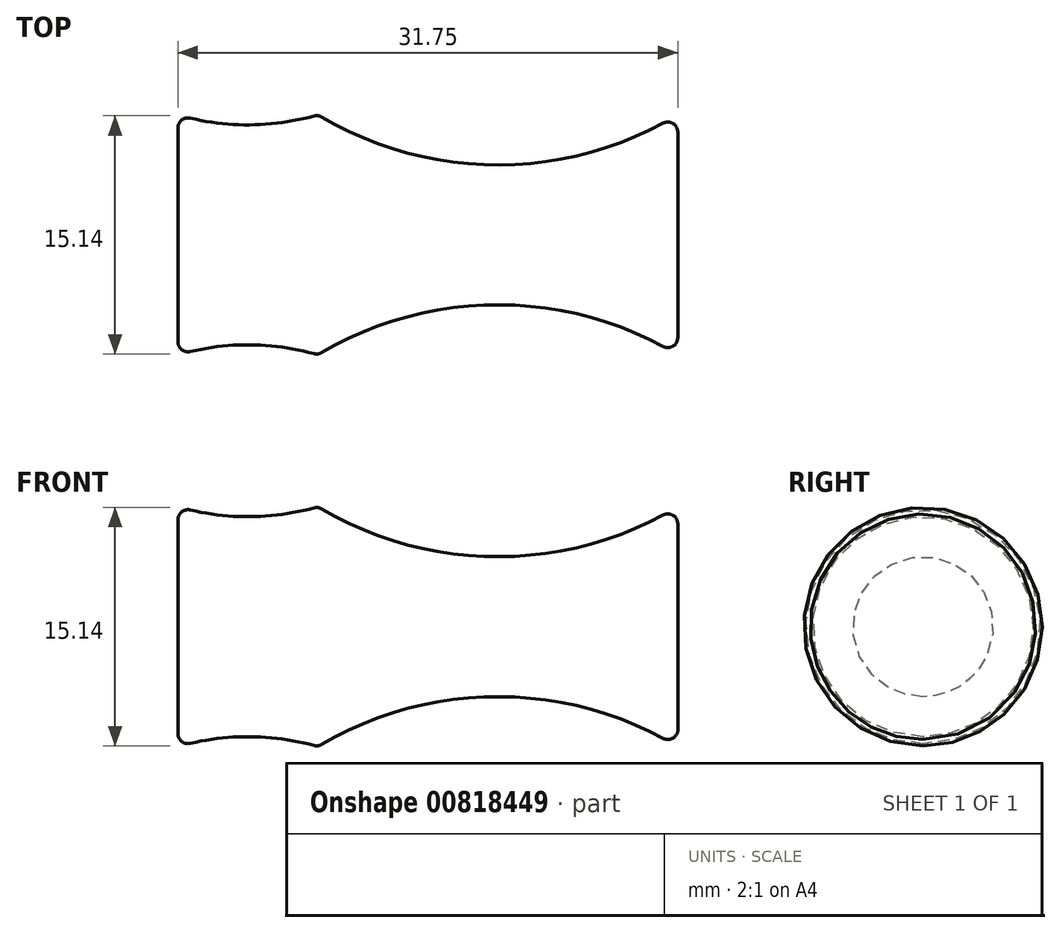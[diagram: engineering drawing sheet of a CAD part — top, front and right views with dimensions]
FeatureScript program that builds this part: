
annotation { "Feature Type Name" : "Feature", "Feature Type Description" : "" }
export const myFeature = defineFeature(function(context is Context, id is Id, definition is map)
    precondition{}
    {
        {
            var Q0;
            Q0=qCreatedBy(makeId("Top.planeOp"),FACE);
            var sketch = newSketch(context, id + "F0", { "sketchPlane" : qUnion([Q0])});
            skLineSegment(sketch, "E0", {"start": v(0, 0) * mm, "end": v(-31.75, 0) * mm});
            skLineSegment(sketch, "E1", {"start": v(-31.75, 0) * mm, "end": v(-31.75, 6.8) * mm});
            skArc(sketch, "E2", {"start": v(-30.97, 7.41) * mm, "mid": v(-27.03, 6.99) * mm, "end": v(-23.12, 7.55) * mm});
            skPoint(sketch, "E3.start.orphan", {"position": v(-27.3, 7.62) * mm});
            skLineSegment(sketch, "E4", {"start": v(0, 0) * mm, "end": v(0, 6.53) * mm});
            skLineSegment(sketch, "E5", {"start": v(-22.86, 7.62) * mm, "end": v(0, 7.62) * mm, "construction": true});
            skLineSegment(sketch, "E6", {"start": v(-11.43, 7.62) * mm, "end": v(-11.43, 4.44) * mm, "construction": true});
            skArc(sketch, "E7", {"start": v(-22.63, 7.48) * mm, "mid": v(-11.83, 4.45) * mm, "end": v(-0.94, 7.09) * mm});
            skPoint(sketch, "E8.visualSharp", {"position": v(0, 7.62) * mm});
            skArc(sketch, "E8.filletArc", {"start": v(0, 6.53) * mm, "mid": v(-0.3, 7.07) * mm, "end": v(-0.94, 7.09) * mm});
            skPoint(sketch, "E9.visualSharp", {"position": v(-22.86, 7.62) * mm});
            skArc(sketch, "E9.filletArc", {"start": v(-22.63, 7.48) * mm, "mid": v(-22.87, 7.56) * mm, "end": v(-23.12, 7.55) * mm});
            skPoint(sketch, "E10.visualSharp", {"position": v(-31.75, 7.62) * mm});
            skArc(sketch, "E10.filletArc", {"start": v(-30.97, 7.41) * mm, "mid": v(-31.5, 7.3) * mm, "end": v(-31.75, 6.8) * mm});
            skSolve(sketch);
        }
        {
            var Q0;
            Q0=makeQuery(id+"F0.imprint","IMPRINT",FACE,{"disambiguationData":[TD([[makeQuery(id+"F0.imprint","IMPRINT",EDGE,{"derivedFrom":sQuery(id+"F0.wireOp",EDGE,"E0")}),-1.0]])]});
            var Q1;
            Q1=sQuery(id+"F0.wireOp",EDGE,"E0");
            revolve(context, id + "F1", {"surfaceOperationType" : NewSurfaceOperationType.NEW, "entities" : qUnion([Q0]), "axis" : qUnion([Q1]), "revolveType" : RevolveType.FULL});
        }
    });
